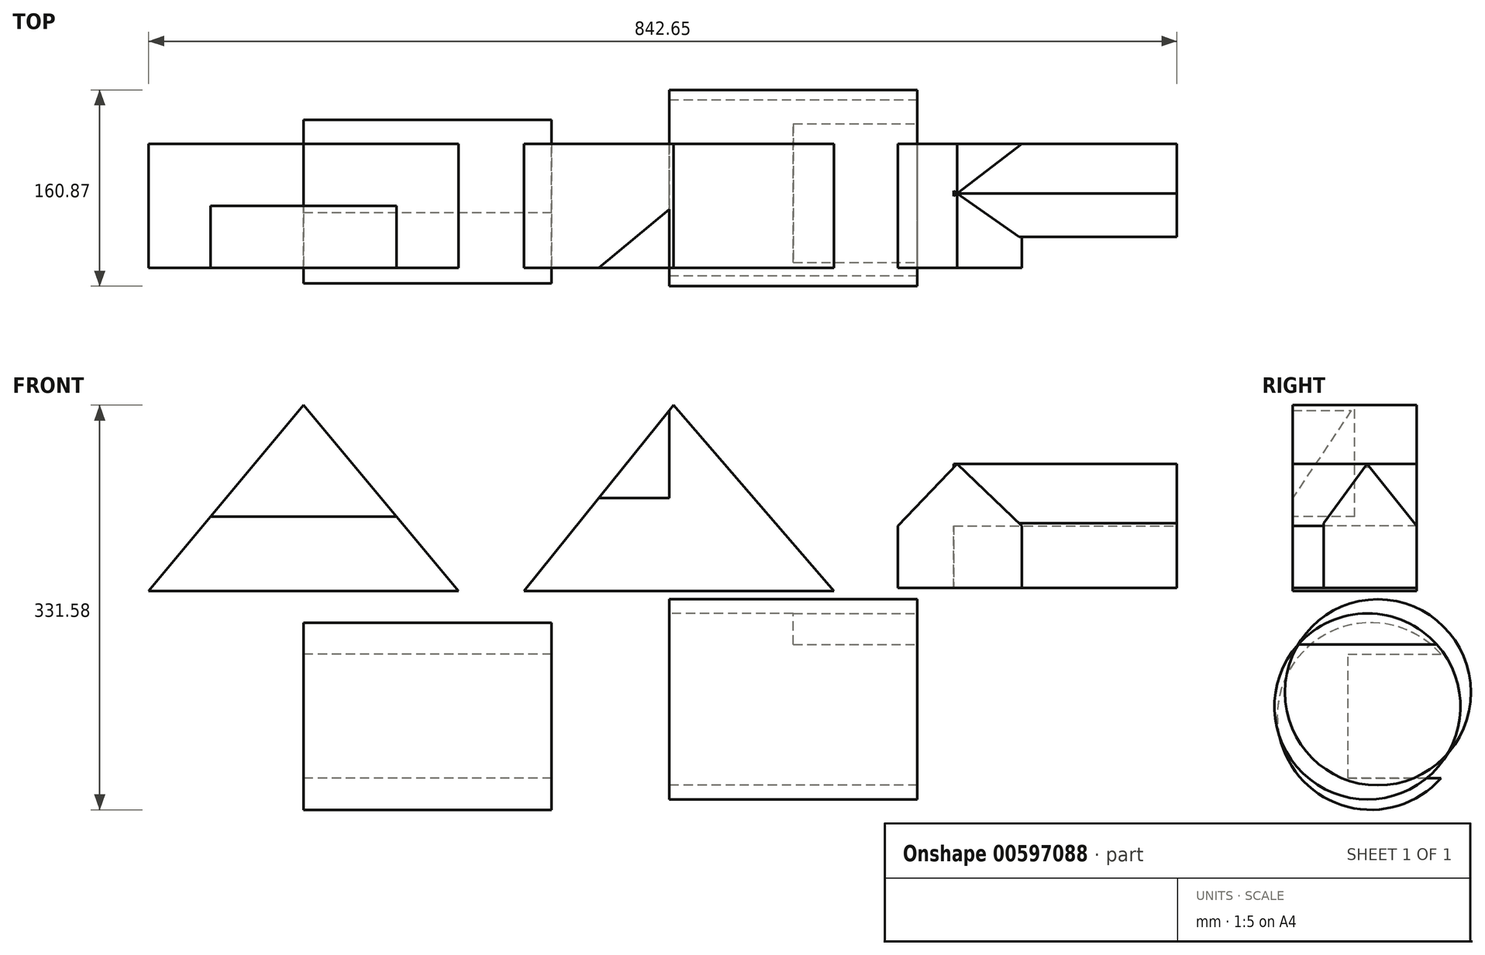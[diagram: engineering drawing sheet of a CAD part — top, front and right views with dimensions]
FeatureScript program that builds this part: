
annotation { "Feature Type Name" : "Feature", "Feature Type Description" : "" }
export const myFeature = defineFeature(function(context is Context, id is Id, definition is map)
    precondition{}
    {
        {
            var Q0;
            Q0=qCreatedBy(makeId("Front.planeOp"),FACE);
            var sketch = newSketch(context, id + "F0", { "sketchPlane" : qUnion([Q0])});
            skLineSegment(sketch, "E0", {"start": v(-127, -152.4) * mm, "end": v(127, -152.4) * mm});
            skLineSegment(sketch, "E1", {"start": v(-127, -152.4) * mm, "end": v(0, 0) * mm});
            skLineSegment(sketch, "E2", {"start": v(0, 0) * mm, "end": v(127, -152.4) * mm});
            skSolve(sketch);
        }
        {
            var Q0;
            Q0=makeQuery(id+"F0.imprint","IMPRINT",FACE,{"disambiguationData":[TD([[makeQuery(id+"F0.imprint","IMPRINT",EDGE,{"derivedFrom":sQuery(id+"F0.wireOp",EDGE,"E0")}),1.0]])]});
            extrude(context, id + "F1", {"entities" : qUnion([Q0]), "oppositeDirection" : true, "depth" : 101.6 * mm, "offsetDistance" : 25.4 * mm});
        }
        {
            var Q0;
            Q0=makeQuery(id+"F1.opExtrude","CAP_FACE",FACE,{"disambiguationData":[OSD([sQuery(id+"F0.wireOp",EDGE,"E0"),sQuery(id+"F0.wireOp",EDGE,"E1"),sQuery(id+"F0.wireOp",EDGE,"E2")])],"isStart":true});
            var sketch = newSketch(context, id + "F2", { "sketchPlane" : qUnion([Q0])});
            skLineSegment(sketch, "E3", {"start": v(0, 0) * mm, "end": v(-76.2, -91.44) * mm});
            skLineSegment(sketch, "E4", {"start": v(-76.2, -91.44) * mm, "end": v(76.2, -91.44) * mm});
            skLineSegment(sketch, "E5", {"start": v(76.2, -91.44) * mm, "end": v(0, 0) * mm});
            skSolve(sketch);
        }
        {
            var Q0;
            Q0 = qSketchRegion(id + "F2", true);
            extrude(context, id + "F3", {"entities" : qUnion([Q0]), "operationType" : NewBodyOperationType.REMOVE, "oppositeDirection" : true, "depth" : 50.8 * mm, "offsetDistance" : 25.4 * mm});
        }
        {
            var Q0;
            Q0=qCreatedBy(makeId("Front.planeOp"),FACE);
            var sketch = newSketch(context, id + "F4", { "sketchPlane" : qUnion([Q0])});
            skLineSegment(sketch, "E6", {"start": v(180.46, -152.4) * mm, "end": v(434.46, -152.4) * mm});
            skLineSegment(sketch, "E7", {"start": v(434.46, -152.4) * mm, "end": v(303.26, 0) * mm});
            skLineSegment(sketch, "E8", {"start": v(303.26, 0) * mm, "end": v(180.46, -152.4) * mm});
            skSolve(sketch);
        }
        {
            var Q0;
            Q0 = qSketchRegion(id + "F4", true);
            extrude(context, id + "F5", {"entities" : qUnion([Q0]), "oppositeDirection" : true, "depth" : 101.6 * mm, "offsetDistance" : 25.4 * mm});
        }
        {
            var Q0;
            Q0=qCreatedBy(makeId("Right.planeOp"),FACE);
            cPlane(context, id + "F6", {"entities" : qUnion([Q0]), "cplaneType" : CPlaneType.OFFSET, "offset" : 299.72 * mm, "width" : 152.4 * mm, "height" : 152.4 * mm});
        }
        {
            var Q0;
            Q0=qCreatedBy(id+"F6.planeOp",FACE);
            var sketch = newSketch(context, id + "F7", { "sketchPlane" : qUnion([Q0])});
            skLineSegment(sketch, "E9", {"start": v(0, 0) * mm, "end": v(50.8, 0) * mm});
            skLineSegment(sketch, "E10", {"start": v(50.8, 0) * mm, "end": v(0, 0) * mm});
            skLineSegment(sketch, "E11", {"start": v(0, 0) * mm, "end": v(0, -76.2) * mm});
            skLineSegment(sketch, "E12", {"start": v(0, -76.2) * mm, "end": v(50.8, 0) * mm});
            skSolve(sketch);
        }
        {
            var Q0;
            Q0 = qSketchRegion(id + "F7", true);
            extrude(context, id + "F8", {"entities" : qUnion([Q0]), "operationType" : NewBodyOperationType.REMOVE, "oppositeDirection" : true, "depth" : 220.98 * mm, "offsetDistance" : 25.4 * mm});
        }
        {
            var Q0;
            Q0=qCreatedBy(makeId("Front.planeOp"),FACE);
            var sketch = newSketch(context, id + "F9", { "sketchPlane" : qUnion([Q0])});
            skLineSegment(sketch, "E13", {"start": v(487.05, -149.7) * mm, "end": v(588.65, -149.7) * mm});
            skLineSegment(sketch, "E14", {"start": v(588.65, -149.7) * mm, "end": v(588.65, -98.9) * mm});
            skLineSegment(sketch, "E15", {"start": v(487.05, -149.7) * mm, "end": v(487.05, -98.9) * mm});
            skLineSegment(sketch, "E16", {"start": v(487.05, -98.9) * mm, "end": v(535.55, -48.1) * mm});
            skLineSegment(sketch, "E17", {"start": v(535.55, -48.1) * mm, "end": v(588.65, -98.9) * mm});
            skSolve(sketch);
        }
        {
            var Q0;
            Q0 = qSketchRegion(id + "F9", true);
            extrude(context, id + "F10", {"entities" : qUnion([Q0]), "oppositeDirection" : true, "depth" : 101.6 * mm, "offsetDistance" : 25.4 * mm});
        }
        {
            var Q0;
            Q0=makeQuery(id+"F10.opExtrude","SWEPT_FACE",FACE,{"disambiguationData":[OSD([sQuery(id+"F9.wireOp",EDGE,"E14")])]});
            cPlane(context, id + "F11", {"entities" : qUnion([Q0]), "cplaneType" : CPlaneType.OFFSET, "offset" : 127 * mm, "width" : 152.4 * mm, "height" : 152.4 * mm});
        }
        {
            var Q0;
            Q0=qCreatedBy(id+"F11.planeOp",FACE);
            var sketch = newSketch(context, id + "F12", { "sketchPlane" : qUnion([Q0])});
            skLineSegment(sketch, "E18", {"start": v(101.63, -149.7) * mm, "end": v(25.43, -149.7) * mm});
            skLineSegment(sketch, "E19", {"start": v(101.63, -98.9) * mm, "end": v(101.63, -149.7) * mm});
            skLineSegment(sketch, "E20", {"start": v(25.43, -96.72) * mm, "end": v(60.96, -48.1) * mm});
            skLineSegment(sketch, "E21", {"start": v(60.96, -48.1) * mm, "end": v(101.63, -98.9) * mm});
            skLineSegment(sketch, "E22", {"start": v(25.43, -96.72) * mm, "end": v(25.43, -149.7) * mm});
            skSolve(sketch);
        }
        {
            var Q0;
            Q0 = qSketchRegion(id + "F12", true);
            extrude(context, id + "F13", {"entities" : qUnion([Q0]), "operationType" : NewBodyOperationType.ADD, "oppositeDirection" : true, "depth" : 182.88 * mm, "offsetDistance" : 25.4 * mm});
        }
        {
            var Q0;
            Q0=qCreatedBy(id+"F6.planeOp",FACE);
            var sketch = newSketch(context, id + "F14", { "sketchPlane" : qUnion([Q0])});
            skCircle(sketch, "E23", {"center": v(69.73, -235.3) * mm, "radius": 76.2 * mm});
            skSolve(sketch);
        }
        {
            var Q0;
            Q0 = qSketchRegion(id + "F14", true);
            extrude(context, id + "F15", {"entities" : qUnion([Q0]), "operationType" : NewBodyOperationType.ADD, "depth" : 203.2 * mm, "offsetDistance" : 25.4 * mm});
        }
        {
            var Q0;
            Q0=qCreatedBy(id+"F6.planeOp",FACE);
            var sketch = newSketch(context, id + "F16", { "sketchPlane" : qUnion([Q0])});
            skCircle(sketch, "E24", {"center": v(61.26, -246.9) * mm, "radius": 76.2 * mm});
            skSolve(sketch);
        }
        {
            var Q0;
            Q0 = qSketchRegion(id + "F16", true);
            extrude(context, id + "F17", {"entities" : qUnion([Q0]), "depth" : 203.2 * mm, "offsetDistance" : 25.4 * mm});
        }
        {
            var Q0;
            Q0=makeQuery(id+"F17.opExtrude","CAP_FACE",FACE,{"disambiguationData":[OSD([sQuery(id+"F16.wireOp",EDGE,"E24")])],"isStart":false});
            var sketch = newSketch(context, id + "F18", { "sketchPlane" : qUnion([Q0])});
            skSolve(sketch);
        }
        {
            var Q0;
            Q0=makeQuery(id+"F18.imprint","IMPRINT",FACE,{"disambiguationData":[TD([[makeQuery(id+"F18.imprint","IMPRINT",EDGE,{"derivedFrom":makeQuery(id+"F17.opExtrude","CAP_EDGE",EDGE,{"disambiguationData":[OSD([sQuery(id+"F16.wireOp",EDGE,"E24")])],"isStart":false})}),1.0]])]});
            var sketch = newSketch(context, id + "F19", { "sketchPlane" : qUnion([Q0])});
            skLineSegment(sketch, "E25", {"start": v(3.99, -196.1) * mm, "end": v(120.5, -196.1) * mm});
            skSolve(sketch);
        }
        {
            var Q0;
            {var subQ0=sQuery(id+"F19.wireOp",EDGE,"E25");var subQ1=makeQuery(id+"F18.imprint","IMPRINT",EDGE,{"derivedFrom":makeQuery(id+"F17.opExtrude","CAP_EDGE",EDGE,{"disambiguationData":[OSD([sQuery(id+"F16.wireOp",EDGE,"E24")])],"isStart":false})});var subQ2=makeQuery(id+"F19.imprint","INTERSECT",VERTEX,{"disambiguationData":[OD(0.0)],"derivedFrom":[subQ1,subQ0]});Q0=makeQuery(id+"F19.imprint","IMPRINT",FACE,{"disambiguationData":[TD([[makeQuery(id+"F19.imprint","IMPRINT",EDGE,{"disambiguationData":[TD([[subQ2,-1.0]])],"derivedFrom":subQ0}),1.0]])]});}
            extrude(context, id + "F20", {"entities" : qUnion([Q0]), "operationType" : NewBodyOperationType.REMOVE, "oppositeDirection" : true, "depth" : 101.6 * mm, "offsetDistance" : 25.4 * mm});
        }
        {
            var Q0;
            Q0=qCreatedBy(makeId("Right.planeOp"),FACE);
            var sketch = newSketch(context, id + "F21", { "sketchPlane" : qUnion([Q0])});
            skCircle(sketch, "E26", {"center": v(64.01, -254.9) * mm, "radius": 76.67 * mm});
            skSolve(sketch);
        }
        {
            var Q0;
            Q0 = qSketchRegion(id + "F21", true);
            extrude(context, id + "F22", {"entities" : qUnion([Q0]), "depth" : 203.2 * mm, "offsetDistance" : 25.4 * mm});
        }
        {
            var Q0;
            Q0=makeQuery(id+"F22.opExtrude","CAP_FACE",FACE,{"disambiguationData":[OSD([sQuery(id+"F21.wireOp",EDGE,"E26")])],"isStart":true});
            var sketch = newSketch(context, id + "F23", { "sketchPlane" : qUnion([Q0])});
            skLineSegment(sketch, "E27", {"start": v(-121.44, -204.1) * mm, "end": v(-45.24, -204.1) * mm});
            skLineSegment(sketch, "E28", {"start": v(-45.24, -204.1) * mm, "end": v(-45.24, -305.7) * mm});
            skLineSegment(sketch, "E29", {"start": v(-45.24, -305.7) * mm, "end": v(-121.44, -305.7) * mm});
            skSolve(sketch);
        }
        {
            var Q0;
            Q0 = qSketchRegion(id + "F23", true);
            var Q1;
            {var subQ0=sQuery(id+"F23.wireOp",EDGE,"E27");Q1=makeQuery(id+"F23.imprint","IMPRINT",FACE,{"disambiguationData":[TD([[makeQuery(id+"F23.imprint","IMPRINT",EDGE,{"derivedFrom":subQ0}),-1.0]])]});}
            extrude(context, id + "F24", {"entities" : qUnion([Q0, Q1]), "operationType" : NewBodyOperationType.REMOVE, "oppositeDirection" : true, "depth" : 261.62 * mm, "offsetDistance" : 25.4 * mm});
        }
    });
